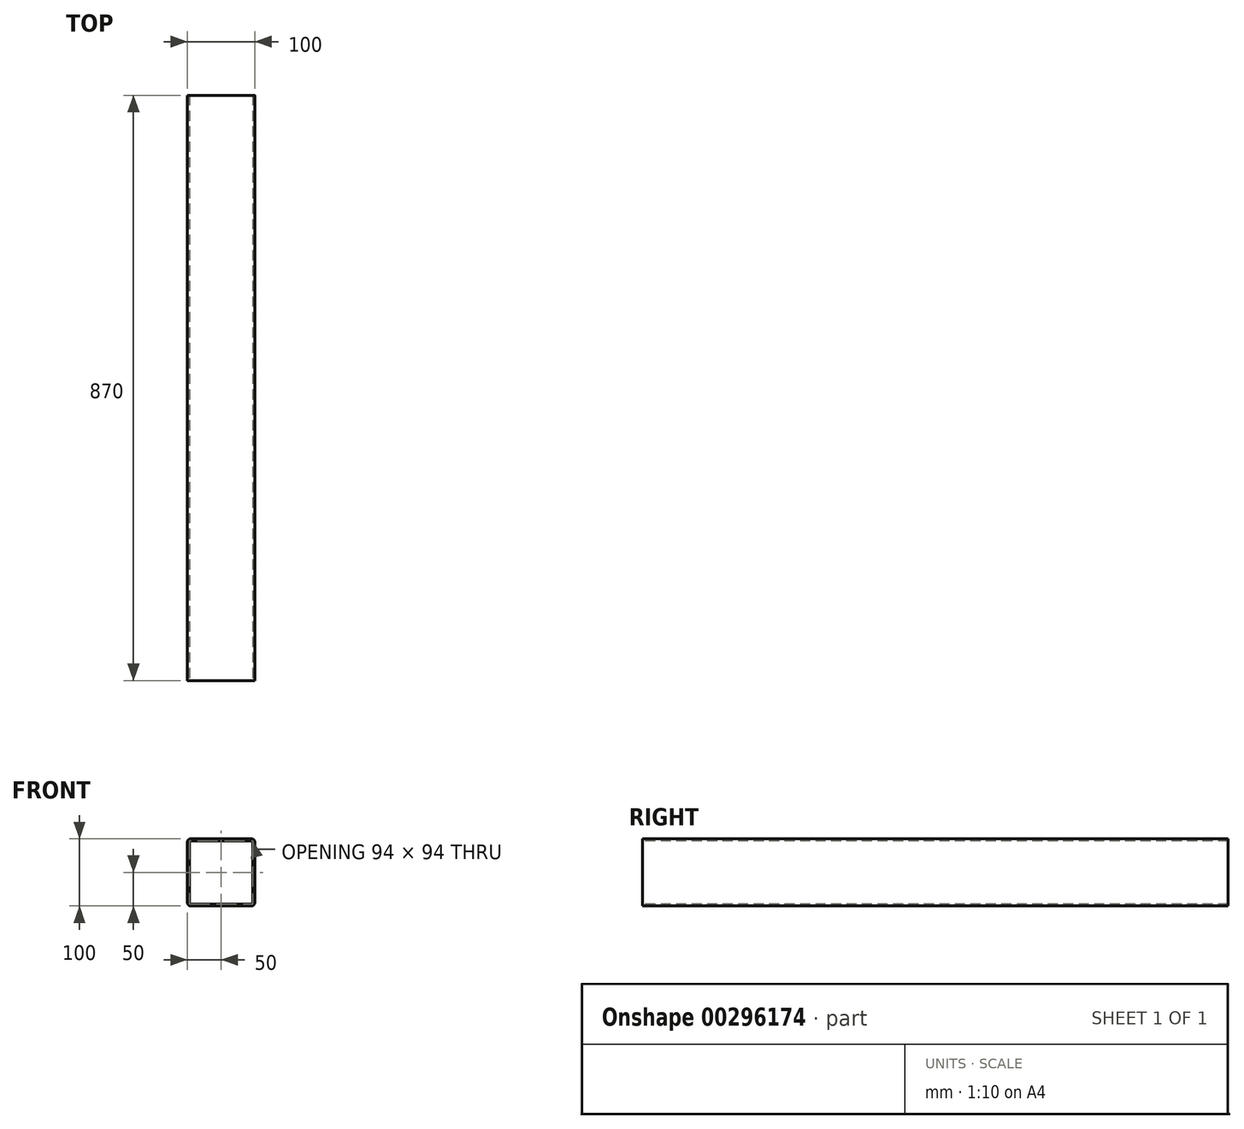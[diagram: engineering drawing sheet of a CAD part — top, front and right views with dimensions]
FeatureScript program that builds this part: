
annotation { "Feature Type Name" : "Feature", "Feature Type Description" : "" }
export const myFeature = defineFeature(function(context is Context, id is Id, definition is map)
    precondition{}
    {
        {
            var Q0;
            Q0=qCreatedBy(makeId("Front.planeOp"),FACE);
            var sketch = newSketch(context, id + "F0", { "sketchPlane" : qUnion([Q0])});
            skLineSegment(sketch, "E0.bottom", {"start": v(45, 50) * mm, "end": v(-45, 50) * mm});
            skLineSegment(sketch, "E0.top", {"start": v(45, -50) * mm, "end": v(-45, -50) * mm});
            skLineSegment(sketch, "E0.left", {"start": v(50, 45) * mm, "end": v(50, -45) * mm});
            skLineSegment(sketch, "E0.right", {"start": v(-50, 45) * mm, "end": v(-50, -45) * mm});
            skPoint(sketch, "E0.middle", {"position": v(0, 0) * mm});
            skPoint(sketch, "E1.visualSharp", {"position": v(-50, 50) * mm});
            skArc(sketch, "E1.filletArc", {"start": v(-45, 50) * mm, "mid": v(-48.54, 48.54) * mm, "end": v(-50, 45) * mm});
            skPoint(sketch, "E2.visualSharp", {"position": v(50, 50) * mm});
            skArc(sketch, "E2.filletArc", {"start": v(50, 45) * mm, "mid": v(48.54, 48.54) * mm, "end": v(45, 50) * mm});
            skPoint(sketch, "E3.visualSharp", {"position": v(50, -50) * mm});
            skArc(sketch, "E3.filletArc", {"start": v(45, -50) * mm, "mid": v(48.54, -48.54) * mm, "end": v(50, -45) * mm});
            skPoint(sketch, "E4.visualSharp", {"position": v(-50, -50) * mm});
            skArc(sketch, "E4.filletArc", {"start": v(-50, -45) * mm, "mid": v(-48.54, -48.54) * mm, "end": v(-45, -50) * mm});
            skArc(sketch, "E5.0", {"start": v(-45, 47) * mm, "mid": v(-46.41, 46.41) * mm, "end": v(-47, 45) * mm});
            skLineSegment(sketch, "E5.1", {"start": v(45, 47) * mm, "end": v(-45, 47) * mm});
            skLineSegment(sketch, "E5.2", {"start": v(-47, 45) * mm, "end": v(-47, -45) * mm});
            skArc(sketch, "E5.3", {"start": v(47, 45) * mm, "mid": v(46.41, 46.41) * mm, "end": v(45, 47) * mm});
            skArc(sketch, "E5.4", {"start": v(-47, -45) * mm, "mid": v(-46.41, -46.41) * mm, "end": v(-45, -47) * mm});
            skLineSegment(sketch, "E5.5", {"start": v(45, -47) * mm, "end": v(-45, -47) * mm});
            skArc(sketch, "E5.6", {"start": v(45, -47) * mm, "mid": v(46.41, -46.41) * mm, "end": v(47, -45) * mm});
            skLineSegment(sketch, "E5.7", {"start": v(47, 45) * mm, "end": v(47, -45) * mm});
            skSolve(sketch);
        }
        {
            var Q0;
            Q0=makeQuery(id+"F0.imprint","IMPRINT",FACE,{"disambiguationData":[TD([[makeQuery(id+"F0.imprint","IMPRINT",EDGE,{"derivedFrom":sQuery(id+"F0.wireOp",EDGE,"E0.bottom")}),1.0]])]});
            extrude(context, id + "F1", {"entities" : qUnion([Q0]), "oppositeDirection" : true, "depth" : (900 - 2 * 15) * mm});
        }
    });
